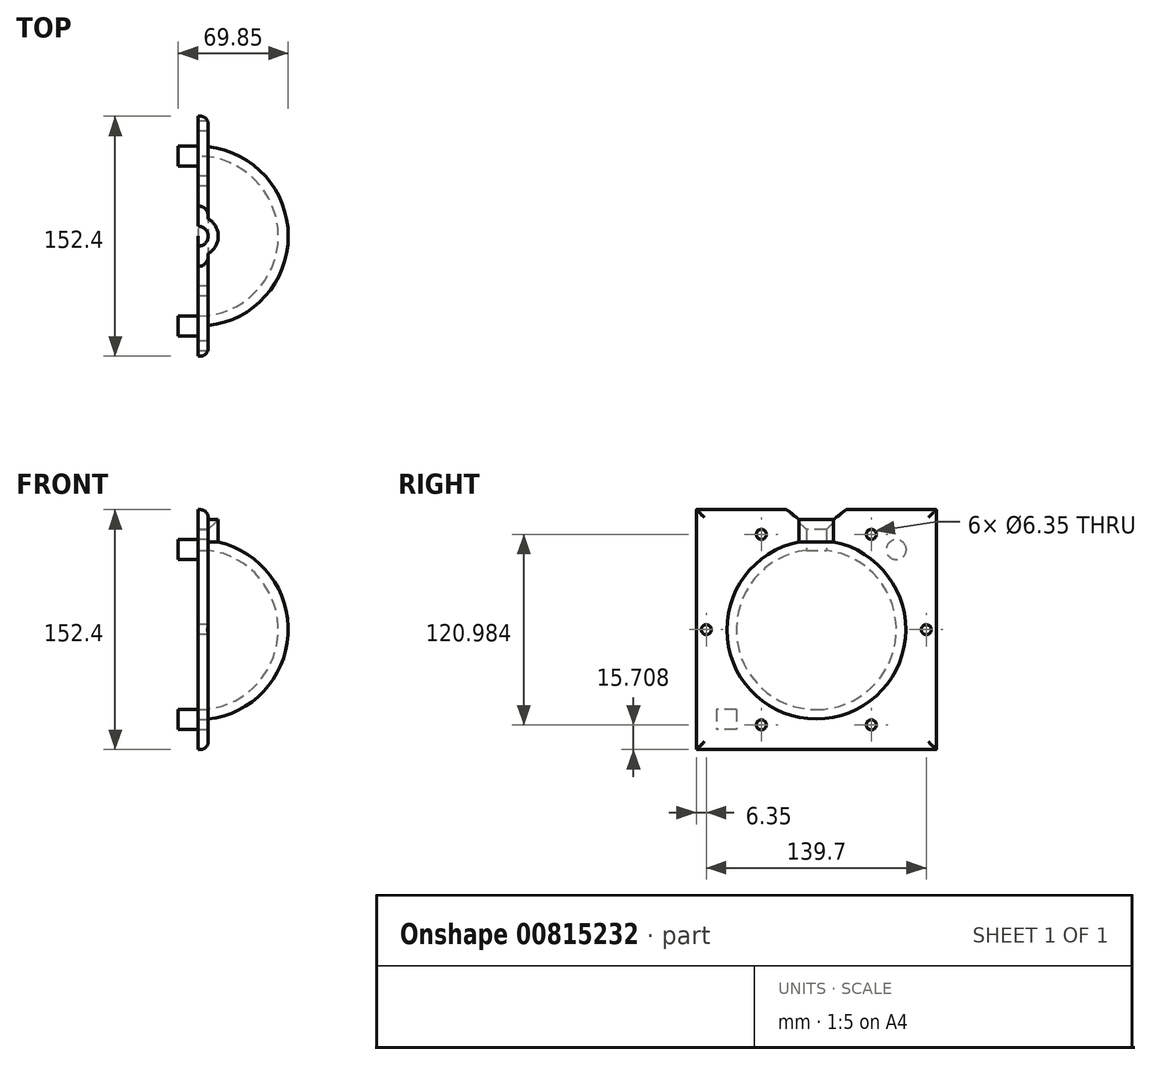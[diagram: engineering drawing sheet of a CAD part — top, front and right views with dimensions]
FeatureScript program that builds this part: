
annotation { "Feature Type Name" : "Feature", "Feature Type Description" : "" }
export const myFeature = defineFeature(function(context is Context, id is Id, definition is map)
    precondition{}
    {
        {
            var Q0;
            Q0=qCreatedBy(makeId("Right.planeOp"),FACE);
            var sketch = newSketch(context, id + "F0", { "sketchPlane" : qUnion([Q0])});
            skCircle(sketch, "E0", {"center": v(0, 0) * mm, "radius": 50.8 * mm});
            skLineSegment(sketch, "E1", {"start": v(0, -50.8) * mm, "end": v(0, -76.2) * mm});
            skLineSegment(sketch, "E2", {"start": v(0, -76.2) * mm, "end": v(76.2, -76.2) * mm});
            skLineSegment(sketch, "E3", {"start": v(76.2, -76.2) * mm, "end": v(76.2, 76.2) * mm});
            skLineSegment(sketch, "E4", {"start": v(76.2, 76.2) * mm, "end": v(6.35, 76.2) * mm});
            skLineSegment(sketch, "E5", {"start": v(6.35, 76.2) * mm, "end": v(6.35, 50.4) * mm});
            skSolve(sketch);
        }
        {
            var Q0;
            {var subQ0=sQuery(id+"F0.wireOp",EDGE,"E1");Q0=makeQuery(id+"F0.imprint","IMPRINT",FACE,{"disambiguationData":[TD([[makeQuery(id+"F0.imprint","IMPRINT",EDGE,{"derivedFrom":subQ0}),1.0]])]});}
            var Q1;
            Q1=sQuery(id+"F0.wireOp",EDGE,"E1");
            revolve(context, id + "F1", {"surfaceOperationType" : NewSurfaceOperationType.NEW, "entities" : qUnion([Q0]), "axis" : qUnion([Q1]), "revolveType" : RevolveType.ONE_DIRECTION, "angle" : 180 * degree});
        }
        {
            var Q0;
            Q0=makeQuery(id+"F1.opRevolve","CAP_FACE",FACE,{"disambiguationData":[OSD([sQuery(id+"F0.wireOp",EDGE,"E0"),sQuery(id+"F0.wireOp",EDGE,"E1"),sQuery(id+"F0.wireOp",EDGE,"E2"),sQuery(id+"F0.wireOp",EDGE,"E3"),sQuery(id+"F0.wireOp",EDGE,"E4"),sQuery(id+"F0.wireOp",EDGE,"E5")])],"isStart":false});
            var sketch = newSketch(context, id + "F2", { "sketchPlane" : qUnion([Q0])});
            skCircle(sketch, "E6", {"center": v(-50.8, 50.8) * mm, "radius": 6.35 * mm});
            skLineSegment(sketch, "E7.bottom", {"start": v(50.8, -50.8) * mm, "end": v(63.5, -50.8) * mm});
            skLineSegment(sketch, "E7.top", {"start": v(50.8, -63.5) * mm, "end": v(63.5, -63.5) * mm});
            skLineSegment(sketch, "E7.left", {"start": v(50.8, -50.8) * mm, "end": v(50.8, -63.5) * mm});
            skLineSegment(sketch, "E7.right", {"start": v(63.5, -50.8) * mm, "end": v(63.5, -63.5) * mm});
            skCircle(sketch, "E8.MirrorC", {"center": v(50.8, 50.8) * mm, "radius": 6.35 * mm});
            skLineSegment(sketch, "E9.MirrorCS", {"start": v(-50.8, -50.8) * mm, "end": v(-63.5, -50.8) * mm});
            skLineSegment(sketch, "E10.MirrorCS", {"start": v(-63.5, -50.8) * mm, "end": v(-63.5, -63.5) * mm});
            skLineSegment(sketch, "E11.MirrorCS", {"start": v(-50.8, -63.5) * mm, "end": v(-63.5, -63.5) * mm});
            skLineSegment(sketch, "E12.MirrorCS", {"start": v(-50.8, -50.8) * mm, "end": v(-50.8, -63.5) * mm});
            skSolve(sketch);
        }
        {
            var Q0;
            Q0=makeQuery(id+"F2.imprint","IMPRINT",FACE,{"disambiguationData":[TD([[makeQuery(id+"F2.imprint","IMPRINT",EDGE,{"derivedFrom":sQuery(id+"F2.wireOp",EDGE,"E6")}),1.0]])]});
            var Q1;
            Q1=makeQuery(id+"F2.imprint","IMPRINT",FACE,{"disambiguationData":[TD([[makeQuery(id+"F2.imprint","IMPRINT",EDGE,{"derivedFrom":sQuery(id+"F2.wireOp",EDGE,"E7.bottom")}),-1.0]])]});
            extrude(context, id + "F3", {"entities" : qUnion([Q0, Q1]), "operationType" : NewBodyOperationType.ADD, "depth" : 12.7 * mm, "offsetDistance" : 25.4 * mm});
        }
        {
            var Q0;
            Q0=makeQuery(id+"F1.opRevolve","SWEPT_FACE",FACE,{"disambiguationData":[OSD([sQuery(id+"F0.wireOp",EDGE,"E3")])]});
            var Q1;
            Q1=makeQuery(id+"F1.opRevolve","SWEPT_FACE",FACE,{"disambiguationData":[OSD([sQuery(id+"F0.wireOp",EDGE,"E2")])]});
            var Q2;
            Q2=makeQuery(id+"F1.opRevolve","SWEPT_FACE",FACE,{"disambiguationData":[OSD([sQuery(id+"F0.wireOp",EDGE,"E4")])]});
            shell(context, id + "F4", {"entities" : qUnion([Q0, Q1, Q2]), "thickness" : 6.35 * mm});
        }
        {
            var Q0;
            {var subQ0=sQuery(id+"F0.wireOp",EDGE,"E3");Q0=makeQuery(id+"F4.opShell","OFFSET_EDGE",EDGE,{"disambiguationData":[OSD([subQ0]),TDD([makeQuery(id+"F1.opRevolve","CAP_EDGE",EDGE,{"disambiguationData":[OSD([subQ0])],"isStart":false})])]});}
            var Q1;
            Q1=makeQuery(id+"F4.opShell","OFFSET_EDGE",EDGE,{"disambiguationData":[OSD([sQuery(id+"F0.wireOp",EDGE,"E2")])]});
            var Q2;
            {var subQ0=sQuery(id+"F0.wireOp",EDGE,"E3");Q2=makeQuery(id+"F4.opShell","OFFSET_EDGE",EDGE,{"disambiguationData":[OSD([subQ0]),TDD([makeQuery(id+"F1.opRevolve","CAP_EDGE",EDGE,{"disambiguationData":[OSD([subQ0])],"isStart":true})])]});}
            var Q3;
            {var subQ0=sQuery(id+"F0.wireOp",EDGE,"E4");Q3=makeQuery(id+"F4.opShell","OFFSET_EDGE",EDGE,{"disambiguationData":[OSD([subQ0]),TDD([makeQuery(id+"F1.opRevolve","CAP_EDGE",EDGE,{"disambiguationData":[OSD([subQ0])],"isStart":true})])]});}
            var Q4;
            {var subQ0=sQuery(id+"F0.wireOp",EDGE,"E4");Q4=makeQuery(id+"F4.opShell","OFFSET_EDGE",EDGE,{"disambiguationData":[OSD([subQ0]),TDD([makeQuery(id+"F1.opRevolve","CAP_EDGE",EDGE,{"disambiguationData":[OSD([subQ0])],"isStart":false})])]});}
            fillet(context, id + "F5", {"entities" : qUnion([Q0, Q1, Q2, Q3, Q4]), "radius" : 5.08 * mm, "tangentPropagation" : true, "allowEdgeOverflow" : false});
        }
        {
            var Q0;
            Q0=makeQuery(id+"F1.opRevolve","SWEPT_EDGE",EDGE,{"disambiguationData":[OSD([sQuery(id+"F0.wireOp",EDGE,"E4"),sQuery(id+"F0.wireOp",EDGE,"E5")])]});
            chamfer(context, id + "F6", {"entities" : qUnion([Q0]), "width" : 12.7 * mm, "tangentPropagation" : true});
        }
        {
            var Q0;
            Q0=makeQuery(id+"F1.opRevolve","CAP_FACE",FACE,{"disambiguationData":[OSD([sQuery(id+"F0.wireOp",EDGE,"E0"),sQuery(id+"F0.wireOp",EDGE,"E1"),sQuery(id+"F0.wireOp",EDGE,"E2"),sQuery(id+"F0.wireOp",EDGE,"E3"),sQuery(id+"F0.wireOp",EDGE,"E4"),sQuery(id+"F0.wireOp",EDGE,"E5")])],"isStart":false});
            var sketch = newSketch(context, id + "F7", { "sketchPlane" : qUnion([Q0])});
            skCircle(sketch, "E13", {"center": v(0, 0) * mm, "radius": 69.85 * mm});
            skCircle(sketch, "E14", {"center": v(-69.85, 0) * mm, "radius": 3.18 * mm});
            skCircle(sketch, "E15.1.0", {"center": v(-34.93, -60.5) * mm, "radius": 3.18 * mm});
            skCircle(sketch, "E15.2.0", {"center": v(34.92, -60.5) * mm, "radius": 3.17 * mm});
            skCircle(sketch, "E15.3.0", {"center": v(69.85, 0) * mm, "radius": 3.18 * mm});
            skCircle(sketch, "E15.4.0", {"center": v(34.93, 60.5) * mm, "radius": 3.18 * mm});
            skCircle(sketch, "E15.5.0", {"center": v(-34.93, 60.5) * mm, "radius": 3.18 * mm});
            skSolve(sketch);
        }
        {
            var Q0;
            {var subQ0=sQuery(id+"F7.wireOp",EDGE,"E15.6.0");var subQ1=sQuery(id+"F7.wireOp",EDGE,"E13");var subQ2=makeQuery(id+"F7.imprint","INTERSECT",VERTEX,{"disambiguationData":[OD(0.0)],"derivedFrom":[subQ1,subQ0]});Q0=makeQuery(id+"F7.imprint","IMPRINT",FACE,{"disambiguationData":[TD([[makeQuery(id+"F7.imprint","IMPRINT",EDGE,{"disambiguationData":[TD([[subQ2,-1.0]])],"derivedFrom":subQ1}),-1.0]])]});}
            var Q1;
            {var subQ0=sQuery(id+"F7.wireOp",EDGE,"E15.6.0");var subQ1=sQuery(id+"F7.wireOp",EDGE,"E13");var subQ2=makeQuery(id+"F7.imprint","INTERSECT",VERTEX,{"disambiguationData":[OD(0.0)],"derivedFrom":[subQ1,subQ0]});Q1=makeQuery(id+"F7.imprint","IMPRINT",FACE,{"disambiguationData":[TD([[makeQuery(id+"F7.imprint","IMPRINT",EDGE,{"disambiguationData":[TD([[subQ2,-1.0]])],"derivedFrom":subQ1}),1.0]])]});}
            var Q2;
            {var subQ0=sQuery(id+"F7.wireOp",EDGE,"E15.7.0");var subQ1=sQuery(id+"F7.wireOp",EDGE,"E13");var subQ2=makeQuery(id+"F7.imprint","INTERSECT",VERTEX,{"disambiguationData":[OD(0.0)],"derivedFrom":[subQ1,subQ0]});Q2=makeQuery(id+"F7.imprint","IMPRINT",FACE,{"disambiguationData":[TD([[makeQuery(id+"F7.imprint","IMPRINT",EDGE,{"disambiguationData":[TD([[subQ2,-1.0]])],"derivedFrom":subQ1}),-1.0]])]});}
            var Q3;
            {var subQ0=sQuery(id+"F7.wireOp",EDGE,"E15.7.0");var subQ1=sQuery(id+"F7.wireOp",EDGE,"E13");var subQ2=makeQuery(id+"F7.imprint","INTERSECT",VERTEX,{"disambiguationData":[OD(0.0)],"derivedFrom":[subQ1,subQ0]});Q3=makeQuery(id+"F7.imprint","IMPRINT",FACE,{"disambiguationData":[TD([[makeQuery(id+"F7.imprint","IMPRINT",EDGE,{"disambiguationData":[TD([[subQ2,-1.0]])],"derivedFrom":subQ1}),1.0]])]});}
            var Q4;
            {var subQ0=sQuery(id+"F7.wireOp",EDGE,"E15.8.0");var subQ1=sQuery(id+"F7.wireOp",EDGE,"E13");var subQ2=makeQuery(id+"F7.imprint","INTERSECT",VERTEX,{"disambiguationData":[OD(0.0)],"derivedFrom":[subQ1,subQ0]});Q4=makeQuery(id+"F7.imprint","IMPRINT",FACE,{"disambiguationData":[TD([[makeQuery(id+"F7.imprint","IMPRINT",EDGE,{"disambiguationData":[TD([[subQ2,-1.0]])],"derivedFrom":subQ1}),-1.0]])]});}
            var Q5;
            {var subQ0=sQuery(id+"F7.wireOp",EDGE,"E15.8.0");var subQ1=sQuery(id+"F7.wireOp",EDGE,"E13");var subQ2=makeQuery(id+"F7.imprint","INTERSECT",VERTEX,{"disambiguationData":[OD(0.0)],"derivedFrom":[subQ1,subQ0]});Q5=makeQuery(id+"F7.imprint","IMPRINT",FACE,{"disambiguationData":[TD([[makeQuery(id+"F7.imprint","IMPRINT",EDGE,{"disambiguationData":[TD([[subQ2,-1.0]])],"derivedFrom":subQ1}),1.0]])]});}
            var Q6;
            {var subQ0=sQuery(id+"F7.wireOp",EDGE,"E15.9.0");var subQ1=sQuery(id+"F7.wireOp",EDGE,"E13");var subQ2=makeQuery(id+"F7.imprint","INTERSECT",VERTEX,{"disambiguationData":[OD(0.0)],"derivedFrom":[subQ1,subQ0]});Q6=makeQuery(id+"F7.imprint","IMPRINT",FACE,{"disambiguationData":[TD([[makeQuery(id+"F7.imprint","IMPRINT",EDGE,{"disambiguationData":[TD([[subQ2,-1.0]])],"derivedFrom":subQ1}),-1.0]])]});}
            var Q7;
            {var subQ0=sQuery(id+"F7.wireOp",EDGE,"E15.9.0");var subQ1=sQuery(id+"F7.wireOp",EDGE,"E13");var subQ2=makeQuery(id+"F7.imprint","INTERSECT",VERTEX,{"disambiguationData":[OD(0.0)],"derivedFrom":[subQ1,subQ0]});Q7=makeQuery(id+"F7.imprint","IMPRINT",FACE,{"disambiguationData":[TD([[makeQuery(id+"F7.imprint","IMPRINT",EDGE,{"disambiguationData":[TD([[subQ2,-1.0]])],"derivedFrom":subQ1}),1.0]])]});}
            var Q8;
            {var subQ0=sQuery(id+"F7.wireOp",EDGE,"E14");var subQ1=sQuery(id+"F7.wireOp",EDGE,"E13");var subQ2=makeQuery(id+"F7.imprint","INTERSECT",VERTEX,{"disambiguationData":[OD(0.0)],"derivedFrom":[subQ1,subQ0]});Q8=makeQuery(id+"F7.imprint","IMPRINT",FACE,{"disambiguationData":[TD([[makeQuery(id+"F7.imprint","IMPRINT",EDGE,{"disambiguationData":[TD([[subQ2,-1.0]])],"derivedFrom":subQ1}),-1.0]])]});}
            var Q9;
            {var subQ0=sQuery(id+"F7.wireOp",EDGE,"E14");var subQ1=sQuery(id+"F7.wireOp",EDGE,"E13");var subQ2=makeQuery(id+"F7.imprint","INTERSECT",VERTEX,{"disambiguationData":[OD(0.0)],"derivedFrom":[subQ1,subQ0]});Q9=makeQuery(id+"F7.imprint","IMPRINT",FACE,{"disambiguationData":[TD([[makeQuery(id+"F7.imprint","IMPRINT",EDGE,{"disambiguationData":[TD([[subQ2,-1.0]])],"derivedFrom":subQ1}),1.0]])]});}
            var Q10;
            {var subQ0=sQuery(id+"F7.wireOp",EDGE,"E15.1.0");var subQ1=sQuery(id+"F7.wireOp",EDGE,"E13");var subQ2=makeQuery(id+"F7.imprint","INTERSECT",VERTEX,{"disambiguationData":[OD(0.0)],"derivedFrom":[subQ1,subQ0]});Q10=makeQuery(id+"F7.imprint","IMPRINT",FACE,{"disambiguationData":[TD([[makeQuery(id+"F7.imprint","IMPRINT",EDGE,{"disambiguationData":[TD([[subQ2,-1.0]])],"derivedFrom":subQ1}),-1.0]])]});}
            var Q11;
            {var subQ0=sQuery(id+"F7.wireOp",EDGE,"E15.1.0");var subQ1=sQuery(id+"F7.wireOp",EDGE,"E13");var subQ2=makeQuery(id+"F7.imprint","INTERSECT",VERTEX,{"disambiguationData":[OD(0.0)],"derivedFrom":[subQ1,subQ0]});Q11=makeQuery(id+"F7.imprint","IMPRINT",FACE,{"disambiguationData":[TD([[makeQuery(id+"F7.imprint","IMPRINT",EDGE,{"disambiguationData":[TD([[subQ2,-1.0]])],"derivedFrom":subQ1}),1.0]])]});}
            var Q12;
            {var subQ0=sQuery(id+"F7.wireOp",EDGE,"E15.2.0");var subQ1=sQuery(id+"F7.wireOp",EDGE,"E13");var subQ2=makeQuery(id+"F7.imprint","INTERSECT",VERTEX,{"disambiguationData":[OD(0.0)],"derivedFrom":[subQ1,subQ0]});Q12=makeQuery(id+"F7.imprint","IMPRINT",FACE,{"disambiguationData":[TD([[makeQuery(id+"F7.imprint","IMPRINT",EDGE,{"disambiguationData":[TD([[subQ2,-1.0]])],"derivedFrom":subQ1}),-1.0]])]});}
            var Q13;
            {var subQ0=sQuery(id+"F7.wireOp",EDGE,"E15.2.0");var subQ1=sQuery(id+"F7.wireOp",EDGE,"E13");var subQ2=makeQuery(id+"F7.imprint","INTERSECT",VERTEX,{"disambiguationData":[OD(0.0)],"derivedFrom":[subQ1,subQ0]});Q13=makeQuery(id+"F7.imprint","IMPRINT",FACE,{"disambiguationData":[TD([[makeQuery(id+"F7.imprint","IMPRINT",EDGE,{"disambiguationData":[TD([[subQ2,-1.0]])],"derivedFrom":subQ1}),1.0]])]});}
            var Q14;
            {var subQ0=sQuery(id+"F7.wireOp",EDGE,"E15.4.0");var subQ1=sQuery(id+"F7.wireOp",EDGE,"E13");var subQ2=makeQuery(id+"F7.imprint","INTERSECT",VERTEX,{"disambiguationData":[OD(0.0)],"derivedFrom":[subQ1,subQ0]});Q14=makeQuery(id+"F7.imprint","IMPRINT",FACE,{"disambiguationData":[TD([[makeQuery(id+"F7.imprint","IMPRINT",EDGE,{"disambiguationData":[TD([[subQ2,-1.0]])],"derivedFrom":subQ1}),-1.0]])]});}
            var Q15;
            {var subQ0=sQuery(id+"F7.wireOp",EDGE,"E15.4.0");var subQ1=sQuery(id+"F7.wireOp",EDGE,"E13");var subQ2=makeQuery(id+"F7.imprint","INTERSECT",VERTEX,{"disambiguationData":[OD(0.0)],"derivedFrom":[subQ1,subQ0]});Q15=makeQuery(id+"F7.imprint","IMPRINT",FACE,{"disambiguationData":[TD([[makeQuery(id+"F7.imprint","IMPRINT",EDGE,{"disambiguationData":[TD([[subQ2,-1.0]])],"derivedFrom":subQ1}),1.0]])]});}
            var Q16;
            {var subQ0=sQuery(id+"F7.wireOp",EDGE,"E15.5.0");var subQ1=sQuery(id+"F7.wireOp",EDGE,"E13");var subQ2=makeQuery(id+"F7.imprint","INTERSECT",VERTEX,{"disambiguationData":[OD(0.0)],"derivedFrom":[subQ1,subQ0]});Q16=makeQuery(id+"F7.imprint","IMPRINT",FACE,{"disambiguationData":[TD([[makeQuery(id+"F7.imprint","IMPRINT",EDGE,{"disambiguationData":[TD([[subQ2,-1.0]])],"derivedFrom":subQ1}),1.0]])]});}
            var Q17;
            {var subQ0=sQuery(id+"F7.wireOp",EDGE,"E15.5.0");var subQ1=sQuery(id+"F7.wireOp",EDGE,"E13");var subQ2=makeQuery(id+"F7.imprint","INTERSECT",VERTEX,{"disambiguationData":[OD(0.0)],"derivedFrom":[subQ1,subQ0]});Q17=makeQuery(id+"F7.imprint","IMPRINT",FACE,{"disambiguationData":[TD([[makeQuery(id+"F7.imprint","IMPRINT",EDGE,{"disambiguationData":[TD([[subQ2,-1.0]])],"derivedFrom":subQ1}),-1.0]])]});}
            var Q18;
            {var subQ0=sQuery(id+"F7.wireOp",EDGE,"E15.3.0");var subQ1=sQuery(id+"F7.wireOp",EDGE,"E13");var subQ2=makeQuery(id+"F7.imprint","INTERSECT",VERTEX,{"disambiguationData":[OD(0.0)],"derivedFrom":[subQ1,subQ0]});Q18=makeQuery(id+"F7.imprint","IMPRINT",FACE,{"disambiguationData":[TD([[makeQuery(id+"F7.imprint","IMPRINT",EDGE,{"disambiguationData":[TD([[subQ2,1.0]])],"derivedFrom":subQ1}),1.0]])]});}
            var Q19;
            {var subQ0=sQuery(id+"F7.wireOp",EDGE,"E15.3.0");var subQ1=sQuery(id+"F7.wireOp",EDGE,"E13");var subQ2=makeQuery(id+"F7.imprint","INTERSECT",VERTEX,{"disambiguationData":[OD(0.0)],"derivedFrom":[subQ1,subQ0]});Q19=makeQuery(id+"F7.imprint","IMPRINT",FACE,{"disambiguationData":[TD([[makeQuery(id+"F7.imprint","IMPRINT",EDGE,{"disambiguationData":[TD([[subQ2,1.0]])],"derivedFrom":subQ1}),-1.0]])]});}
            extrude(context, id + "F8", {"entities" : qUnion([Q0, Q1, Q2, Q3, Q4, Q5, Q6, Q7, Q8, Q9, Q10, Q11, Q12, Q13, Q14, Q15, Q16, Q17, Q18, Q19]), "operationType" : NewBodyOperationType.REMOVE, "endBound" : BoundingType.THROUGH_ALL, "oppositeDirection" : true, "depth" : 25.4 * mm, "offsetDistance" : 25.4 * mm});
        }
    });
